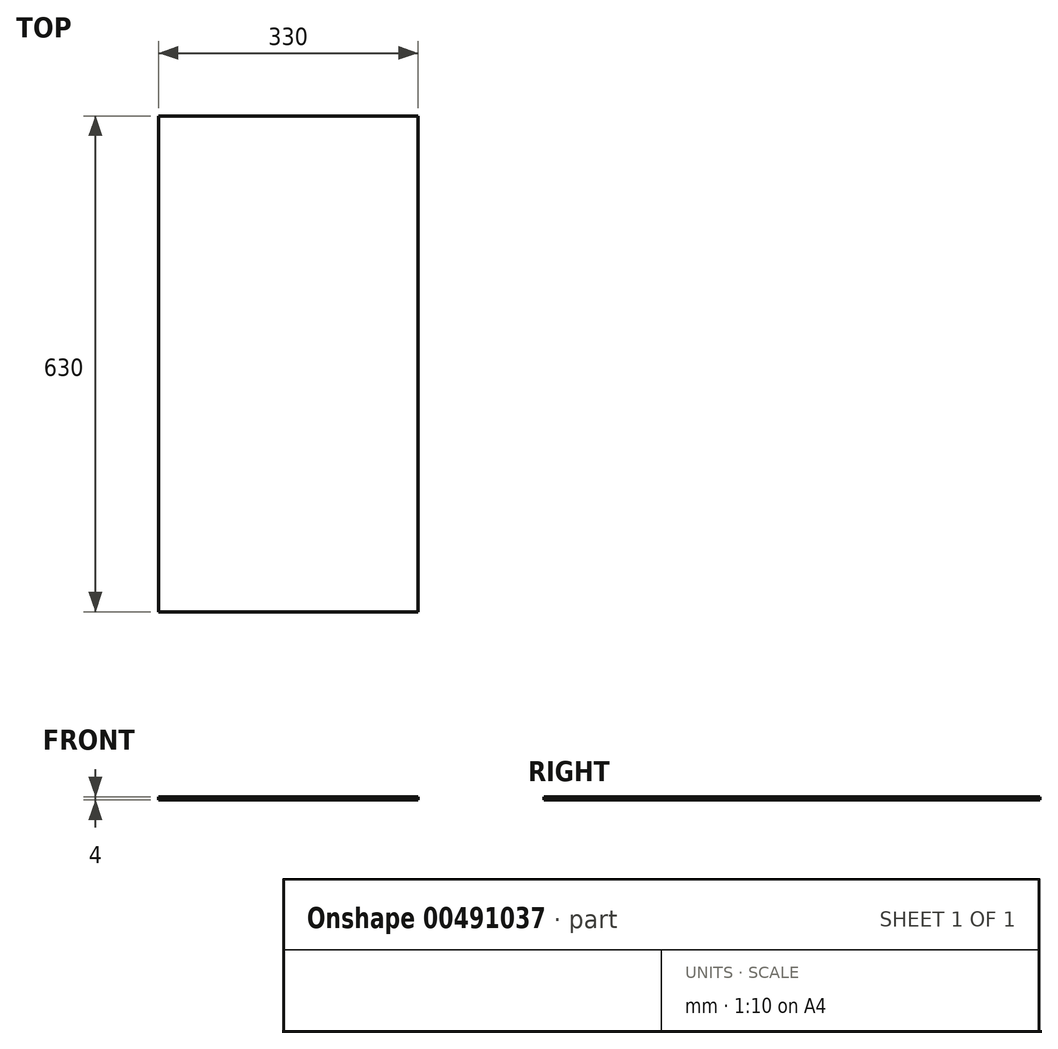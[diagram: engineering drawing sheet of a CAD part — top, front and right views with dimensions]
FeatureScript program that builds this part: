
annotation { "Feature Type Name" : "Feature", "Feature Type Description" : "" }
export const myFeature = defineFeature(function(context is Context, id is Id, definition is map)
    precondition{}
    {
        {
            var Q0;
            Q0=qCreatedBy(makeId("Top.planeOp"),FACE);
            var sketch = newSketch(context, id + "F0", { "sketchPlane" : qUnion([Q0])});
            skLineSegment(sketch, "E0.bottom", {"start": v(0, 0) * mm, "end": v(330, 0) * mm});
            skLineSegment(sketch, "E0.top", {"start": v(0, 630) * mm, "end": v(330, 630) * mm});
            skLineSegment(sketch, "E0.left", {"start": v(0, 0) * mm, "end": v(0, 630) * mm});
            skLineSegment(sketch, "E0.right", {"start": v(330, 0) * mm, "end": v(330, 630) * mm});
            skSolve(sketch);
        }
        {
            var Q0;
            Q0 = qSketchRegion(id + "F0", true);
            extrude(context, id + "F1", {"entities" : qUnion([Q0]), "depth" : 4 * mm, "offsetDistance" : 25 * mm});
        }
    });
